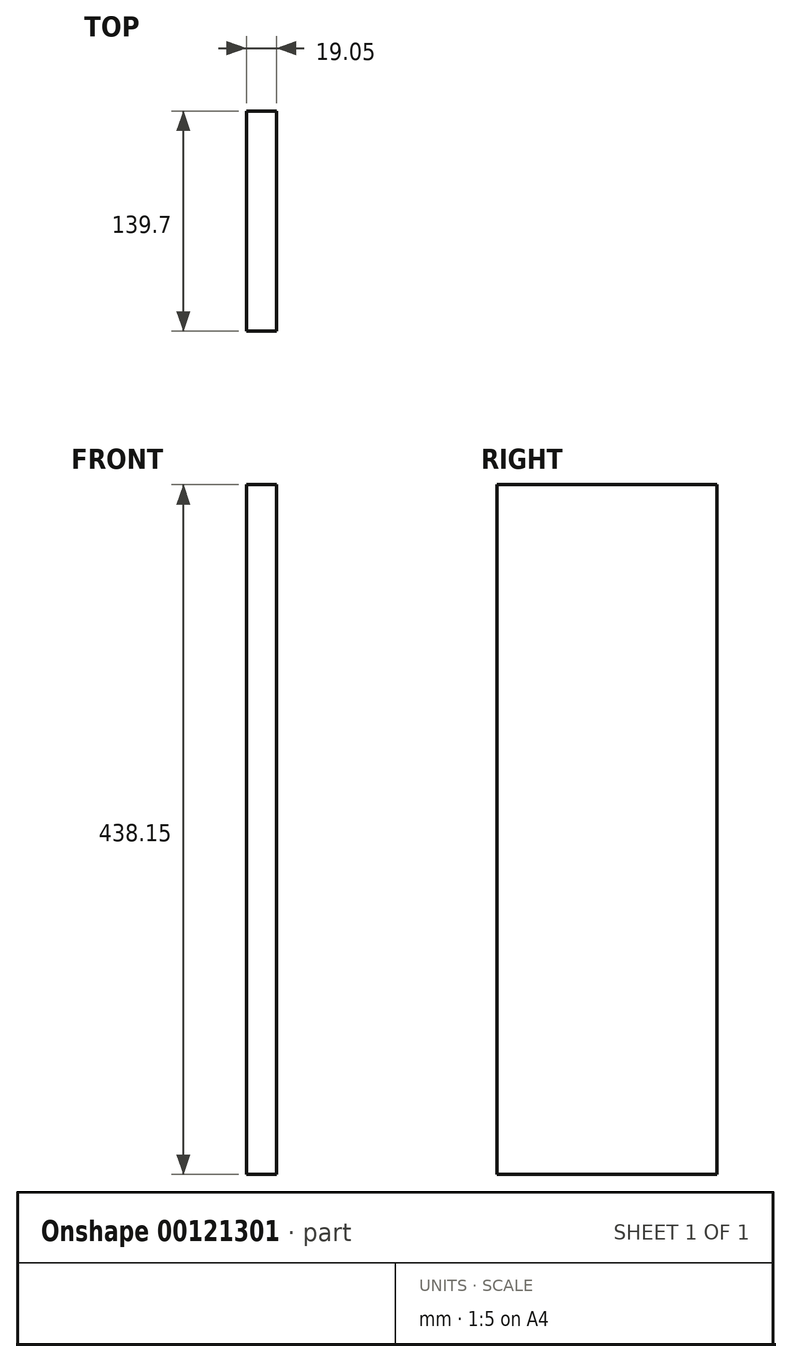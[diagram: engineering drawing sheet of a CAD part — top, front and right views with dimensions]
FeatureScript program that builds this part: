
annotation { "Feature Type Name" : "Feature", "Feature Type Description" : "" }
export const myFeature = defineFeature(function(context is Context, id is Id, definition is map)
    precondition{}
    {
        {
            var Q0;
            Q0=qCreatedBy(makeId("Right.planeOp"),FACE);
            var sketch = newSketch(context, id + "F0", { "sketchPlane" : qUnion([Q0])});
            skLineSegment(sketch, "E0.bottom", {"start": v(0, 0) * mm, "end": v(139.7, 0) * mm});
            skLineSegment(sketch, "E0.top", {"start": v(0, 438.15) * mm, "end": v(139.7, 438.15) * mm});
            skLineSegment(sketch, "E0.left", {"start": v(0, 0) * mm, "end": v(0, 438.15) * mm});
            skLineSegment(sketch, "E0.right", {"start": v(139.7, 0) * mm, "end": v(139.7, 438.15) * mm});
            skSolve(sketch);
        }
        {
            var Q0;
            Q0=makeQuery(id+"F0.imprint","IMPRINT",FACE,{"disambiguationData":[TD([[makeQuery(id+"F0.imprint","IMPRINT",EDGE,{"derivedFrom":sQuery(id+"F0.wireOp",EDGE,"E0.bottom")}),1.0]])]});
            extrude(context, id + "F1", {"entities" : qUnion([Q0]), "depth" : 19.05 * mm});
        }
    });
